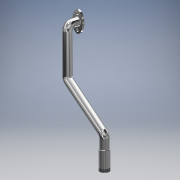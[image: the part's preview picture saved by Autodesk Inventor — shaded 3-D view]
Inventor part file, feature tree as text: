
AUTODESK INVENTOR PART (.ipt)
format: ipt  version: 2018 (Build 220112000, 112)  size: 202,752 bytes
history: native  units: mm
features: sketch x6, extrude x2, plane x2, fillet x2, sweep x1, thread x1
ambient origin geometry x8: Origin, YZ Plane, XZ Plane, XY Plane, X Axis, Y Axis, Z Axis, Center Point
bodies: Solid1 (feature_tree)
feature tree (14):
  extrude  "Extrusion1"  Depth=6.0mm
  sketch  "Sketch2"  dims[d2=7.0mm d3=3.0mm]
  plane  "Work Plane1"
  extrude  "Extrusion2"  Depth=7.0mm
  sketch  "Sketch4"  dims[d11=60.0mm]
  plane  "Work Plane2"
  sketch  "Sketch5"  dims[d12=25.0mm d13=9.0mm d14=7.0mm d15=18.0mm d16=0.0mm d17=8.0mm d18=45.0mm d19=12.0mm d20=12.0mm d21=5.0mm d22=5.0mm d23=5.0mm d24=0.0mm d25=0.0mm d26=0.5mm d27=1.0mm d28=3.0mm d29=15.0mm]
  sweep  "Sweep1"
  fillet  "Fillet1"  Radius=2.0mm
  fillet  "Fillet2"  Radius=10.0mm
  thread  "Thread1"  [1 undecoded]
  sketch  "Sketch1"  dims[d0=10.0mm d1=6.0mm]
  sketch  "Sketch3"  dims[d4=7.0mm d5=2.0mm d6=0.0mm d7=2.0mm d9=10.0mm d10=-100.0mm]
  sketch  "3D Sketch1"
note: 1 required parameter value undecoded (feature->parameter linkage not recoverable at this tier; creation-order binding heuristic only, values carry confidence <= 0.55)
